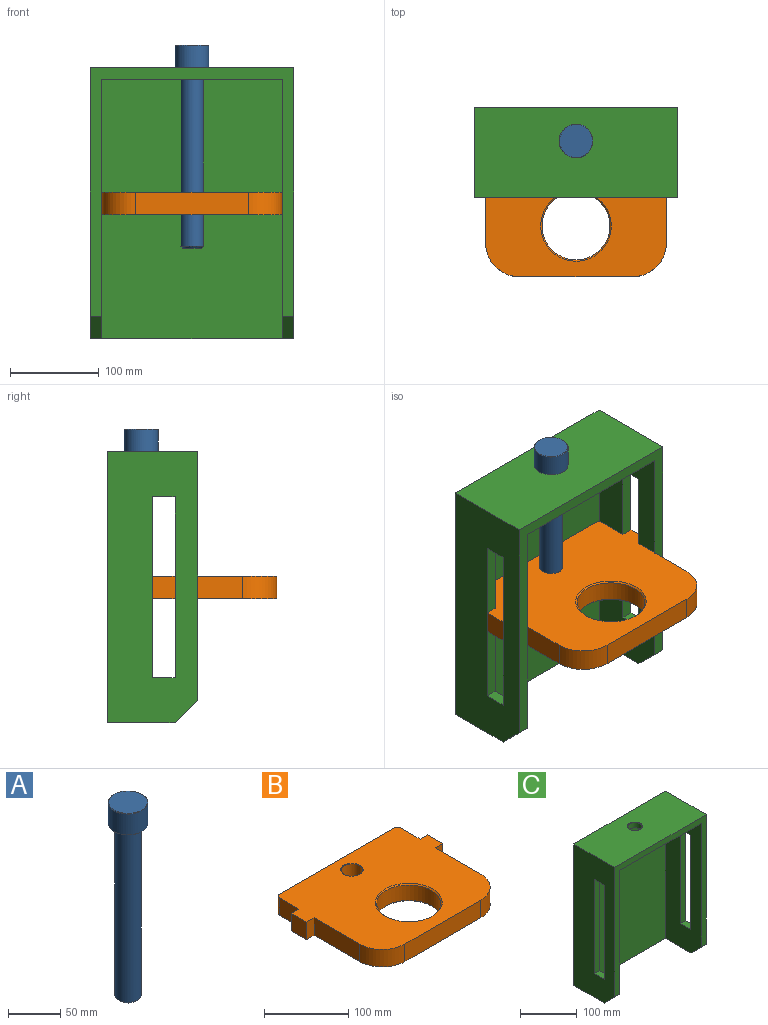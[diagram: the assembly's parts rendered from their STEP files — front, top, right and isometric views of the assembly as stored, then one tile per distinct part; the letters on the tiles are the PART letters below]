
ASSEMBLY  parts=3 mates=2
PART A: 8 faces, bbox 38.1x38.1x228.6 mm
  f0: cylinder r=12.7mm len=200.66mm, axis (0,0,-1), area 16012mm2, adj f2,f5
  f1: plane 20.32x20.32mm, normal (0,0,-1), area 324.3mm2, adj f2
  f2: cone r=12.7mm half-angle=45deg, axis (0,0,1), area 258mm2, adj f0,f1
  f3: cylinder r=19.05mm len=38.1mm, axis (0,0,-1), area 2918.6mm2, adj f6,f7
  f4: plane 37.08x37.08mm, normal (0,0,1), area 1080.1mm2, adj f7
  f5: plane 37.08x37.08mm, normal (0,0,-1), area 573.4mm2, adj f0,f6
  f6: cone r=19.05mm half-angle=45deg, axis (0,0,1), area 84.8mm2, adj f3,f5
  f7: cone r=18.54mm half-angle=45deg, axis (0,0,-1), area 84.8mm2, adj f3,f4
PART B: 24 faces, bbox 228.6x177.8x25.4 mm
  f0: plane 76.2x25.4mm, normal (-1,0,0), area 1935.5mm2, adj f8,f9,f14,f21
  f1: plane 76.2x25.4mm, normal (1,0,0), area 1935.5mm2, adj f8,f9,f15,f20
  f2: plane 33.02x25.4mm, normal (1,0,0), area 838.7mm2, adj f8,f9,f16,f19
  f3: plane 193.04x25.4mm, normal (0,1,0), area 4903.2mm2, adj f8,f9,f16,f17
  f4: plane 33.02x25.4mm, normal (-1,0,0), area 838.7mm2, adj f8,f9,f17,f22
  f5: cylinder r=12.7mm len=25.4mm, axis (0,0,-1), area 1945.8mm2, adj f10,f11
  f6: cylinder r=38.1mm len=76.2mm, axis (0,0,-1), area 5350.8mm2, adj f12,f13
  f7: plane 127x25.4mm, normal (0,-1,0), area 3225.8mm2, adj f8,f9,f14,f15
  f8: plane 228.6x177.8mm, normal (0,0,1), area 30659.5mm2, adj f0,f1,f2,f3,f4,f7,f11,f13
  f9: plane 228.6x177.8mm, normal (0,0,-1), area 30659.5mm2, adj f0,f1,f2,f3,f4,f7,f10,f12
  f10: cone r=13.21mm half-angle=45deg, axis (0,0,-1), area 58.5mm2, adj f5,f9
  f11: cone r=12.7mm half-angle=45deg, axis (0,0,1), area 58.5mm2, adj f5,f8
  f12: cone r=39.62mm half-angle=45deg, axis (0,0,-1), area 526.3mm2, adj f6,f9
  f13: cone r=38.1mm half-angle=45deg, axis (0,0,1), area 526.3mm2, adj f6,f8
  f14: cylinder r=38.1mm len=38.1mm, axis (0,0,-1), area 1520.1mm2, adj f0,f7,f8,f9
  f15: cylinder r=38.1mm len=38.1mm, axis (0,0,1), area 1520.1mm2, adj f1,f7,f8,f9
  f16: cylinder r=5.08mm len=25.4mm, axis (0,0,-1), area 202.7mm2, adj f2,f3,f8,f9
  f17: cylinder r=5.08mm len=25.4mm, axis (0,0,1), area 202.7mm2, adj f3,f4,f8,f9
  f18: plane 25.4x25.4mm, normal (1,0,0), area 645.2mm2, adj f8,f9,f19,f20
  f19: plane 25.4x12.7mm, normal (0,1,0), area 322.6mm2, adj f2,f8,f9,f18
  f20: plane 25.4x12.7mm, normal (0,-1,0), area 322.6mm2, adj f1,f8,f9,f18
  f21: plane 25.4x12.7mm, normal (0,-1,0), area 322.6mm2, adj f0,f8,f9,f23
  f22: plane 25.4x12.7mm, normal (0,1,0), area 322.6mm2, adj f4,f8,f9,f23
  f23: plane 25.4x25.4mm, normal (-1,0,0), area 645.2mm2, adj f8,f9,f21,f22
PART C: 23 faces, bbox 228.6x101.6x304.8 mm
  f0: plane 292.1x203.2mm, normal (0,-1,0), area 59354.7mm2, adj f2,f10,f11,f18
  f1: plane 228.6x101.6mm, normal (0,0,1), area 22677.7mm2, adj f3,f7,f9,f16,f20
  f2: plane 228.6x76.2mm, normal (0,0,-1), area 4516.1mm2, adj f0,f3,f9,f10,f11,f16,f21,f22
  f3: plane 304.8x228.6mm, normal (0,1,0), area 69677.3mm2, adj f1,f2,f9,f16
  f4: plane 203.2x12.7mm, normal (0,1,0), area 2580.6mm2, adj f5,f8,f9,f10
  f5: plane 25.4x12.7mm, normal (0,0,-1), area 322.6mm2, adj f4,f6,f9,f10
  f6: plane 203.2x12.7mm, normal (0,-1,0), area 2580.6mm2, adj f5,f8,f9,f10
  f7: plane 279.4x228.6mm, normal (0,-1,0), area 9677.4mm2, adj f1,f9,f10,f11,f16,f18,f21,f22
  f8: plane 25.4x12.7mm, normal (0,0,1), area 322.6mm2, adj f4,f6,f9,f10
  f9: plane 304.8x101.6mm, normal (1,0,0), area 25483.8mm2, adj f1,f2,f3,f4,f5,f6,f7,f8
  f10: plane 292.1x88.9mm, normal (-1,0,0), area 20483.8mm2, adj f0,f2,f4,f5,f6,f7,f8,f18
  f11: plane 292.1x88.9mm, normal (1,0,0), area 20483.8mm2, adj f0,f2,f7,f12,f13,f14,f15,f18
  f12: plane 25.4x12.7mm, normal (0,0,-1), area 322.6mm2, adj f11,f13,f15,f16
  f13: plane 203.2x12.7mm, normal (0,1,0), area 2580.6mm2, adj f11,f12,f14,f16
  f14: plane 25.4x12.7mm, normal (0,0,1), area 322.6mm2, adj f11,f13,f15,f16
  f15: plane 203.2x12.7mm, normal (0,-1,0), area 2580.6mm2, adj f11,f12,f14,f16
  f16: plane 304.8x101.6mm, normal (-1,0,0), area 25483.8mm2, adj f1,f2,f3,f7,f12,f13,f14,f15
  f17: cylinder r=12.7mm len=25.4mm, axis (0,0,1), area 932.3mm2, adj f19,f20
  f18: plane 203.2x88.9mm, normal (0,0,-1), area 17516.4mm2, adj f0,f7,f10,f11,f19
  f19: cone r=13.21mm half-angle=45deg, axis (0,0,-1), area 58.5mm2, adj f17,f18
  f20: cone r=12.7mm half-angle=45deg, axis (0,0,1), area 58.5mm2, adj f1,f17
  f21: plane 25.4x25.4mm, normal (0,-0.71,-0.71), area 456.2mm2, adj f2,f7,f11,f16
  f22: plane 25.4x25.4mm, normal (0,-0.71,-0.71), area 456.2mm2, adj f2,f7,f9,f10
PLACE A t=(-98.35,-38.43,59.28)mm
PLACE B rot(axis=(0,0.01,-1),0deg) t=(-98.35,-101.93,8.48)mm
PLACE C t=(-98.35,-6.68,8.48)mm fixed
MATE fastened C.f20 <-> A.f0  axis (0,0,1) through (-98.35,-38.43,160.88)mm
MATE slider C.f6 <-> B.f19  axis (0,-1,0) through (9.6,-51.13,8.48)mm
